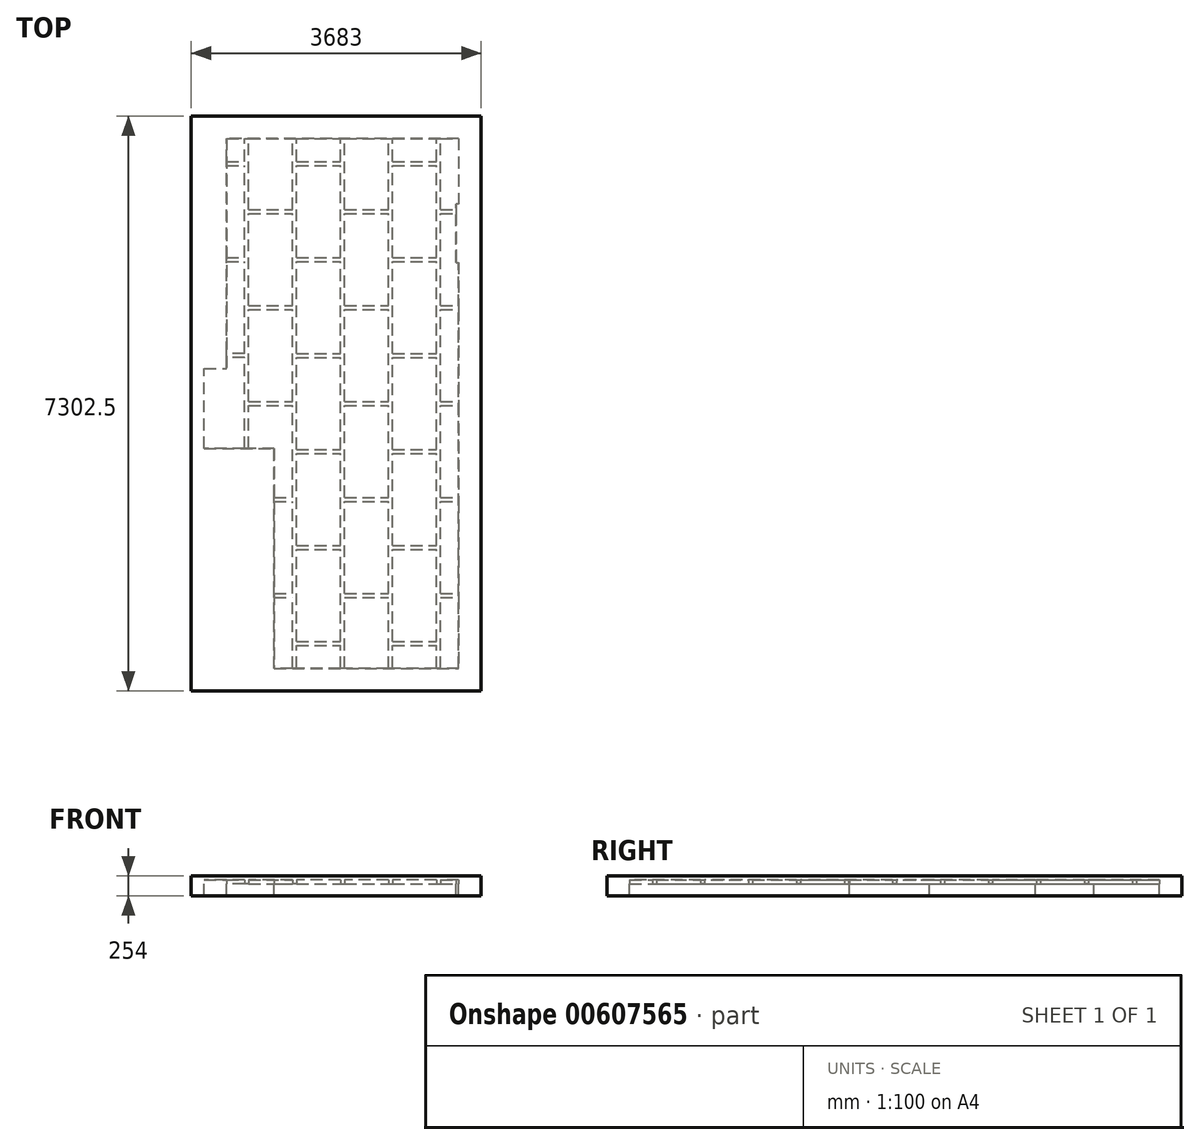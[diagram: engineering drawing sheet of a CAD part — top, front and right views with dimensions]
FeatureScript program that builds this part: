
annotation { "Feature Type Name" : "Feature", "Feature Type Description" : "" }
export const myFeature = defineFeature(function(context is Context, id is Id, definition is map)
    precondition{}
    {
        {
            var Q0;
            Q0=qCreatedBy(makeId("Top.planeOp"),FACE);
            var sketch = newSketch(context, id + "F0", { "sketchPlane" : qUnion([Q0])});
            skLineSegment(sketch, "E0", {"start": v(0, 0) * mm, "end": v(0, 5156.2) * mm});
            skLineSegment(sketch, "E1", {"start": v(0, 5156.2) * mm, "end": v(-34.92, 5156.2) * mm});
            skLineSegment(sketch, "E2", {"start": v(-34.92, 5156.2) * mm, "end": v(-34.92, 5899.15) * mm});
            skLineSegment(sketch, "E3", {"start": v(-34.92, 5899.15) * mm, "end": v(0, 5899.15) * mm});
            skLineSegment(sketch, "E4", {"start": v(0, 5899.15) * mm, "end": v(0, 6731) * mm});
            skLineSegment(sketch, "E5", {"start": v(0, 6731) * mm, "end": v(-2946.4, 6731) * mm});
            skLineSegment(sketch, "E6", {"start": v(-2946.4, 6731) * mm, "end": v(-2946.4, 3810) * mm});
            skLineSegment(sketch, "E7", {"start": v(-2946.4, 3810) * mm, "end": v(-3232.15, 3810) * mm});
            skLineSegment(sketch, "E8", {"start": v(-3232.15, 3810) * mm, "end": v(-3232.15, 2794) * mm});
            skLineSegment(sketch, "E9", {"start": v(-3232.15, 2794) * mm, "end": v(-2343.15, 2794) * mm});
            skLineSegment(sketch, "E10", {"start": v(-2343.15, 2794) * mm, "end": v(-2343.15, 0) * mm});
            skLineSegment(sketch, "E11", {"start": v(-2343.15, 0) * mm, "end": v(0, 0) * mm});
            skLineSegment(sketch, "E12", {"start": v(285.75, 7016.75) * mm, "end": v(285.75, -285.75) * mm});
            skLineSegment(sketch, "E13", {"start": v(285.75, -285.75) * mm, "end": v(-3397.25, -285.75) * mm});
            skLineSegment(sketch, "E14", {"start": v(285.75, 7016.75) * mm, "end": v(-3397.25, 7016.75) * mm});
            skLineSegment(sketch, "E15", {"start": v(-3397.25, 7016.75) * mm, "end": v(-3397.25, -285.75) * mm});
            skSolve(sketch);
        }
        {
            var Q0;
            Q0=makeQuery(id+"F0.imprint","IMPRINT",FACE,{"disambiguationData":[TD([[makeQuery(id+"F0.imprint","IMPRINT",EDGE,{"derivedFrom":sQuery(id+"F0.wireOp",EDGE,"E0")}),-1.0]])]});
            extrude(context, id + "F1", {"entities" : qUnion([Q0]), "oppositeDirection" : true, "depth" : 254 * mm, "offsetDistance" : 25.4 * mm});
        }
        {
            var Q0;
            Q0=qSketchRegion(id+"F0",true);
            var Q1;
            Q1=makeQuery(id+"F0.imprint","IMPRINT",FACE,{"disambiguationData":[TD([[makeQuery(id+"F0.imprint","IMPRINT",EDGE,{"derivedFrom":sQuery(id+"F0.wireOp",EDGE,"E0")}),1.0]])]});
            extrude(context, id + "F2", {"entities" : qUnion([Q0, Q1]), "operationType" : NewBodyOperationType.ADD, "oppositeDirection" : true, "depth" : 101.6 * mm, "offsetDistance" : 25.4 * mm});
        }
        {
            var Q0;
            Q0=makeQuery(id+"F2.opExtrude","CAP_FACE",FACE,{"disambiguationData":[OSD([sQuery(id+"F0.wireOp",EDGE,"E12"),sQuery(id+"F0.wireOp",EDGE,"E13"),sQuery(id+"F0.wireOp",EDGE,"E14"),sQuery(id+"F0.wireOp",EDGE,"E15")])],"isStart":false});
            var sketch = newSketch(context, id + "F3", { "sketchPlane" : qUnion([Q0])});
            skLineSegment(sketch, "E16.bottom", {"start": v(-2060.58, 0) * mm, "end": v(-2111.38, 0) * mm});
            skLineSegment(sketch, "E16.top", {"start": v(-2060.57, -6731) * mm, "end": v(-2111.37, -6731) * mm});
            skLineSegment(sketch, "E16.left", {"start": v(-2060.58, 0) * mm, "end": v(-2060.58, -292.1) * mm});
            skLineSegment(sketch, "E17.bottom", {"start": v(-1450.98, 0) * mm, "end": v(-1501.78, 0) * mm});
            skLineSegment(sketch, "E17.top", {"start": v(-1450.97, -6731) * mm, "end": v(-1501.77, -6731) * mm});
            skLineSegment(sketch, "E17.left", {"start": v(-1450.98, 0) * mm, "end": v(-1450.98, -901.7) * mm});
            skLineSegment(sketch, "E17.right", {"start": v(-1501.78, 0) * mm, "end": v(-1501.78, -292.1) * mm});
            skPoint(sketch, "E18.oppositeSnap0", {"position": v(-892.18, 0) * mm});
            skLineSegment(sketch, "E18.bottom", {"start": v(-841.38, 0) * mm, "end": v(-892.18, 0) * mm});
            skLineSegment(sketch, "E18.top", {"start": v(-841.37, -6731) * mm, "end": v(-892.17, -6731) * mm});
            skLineSegment(sketch, "E18.left", {"start": v(-841.38, 0) * mm, "end": v(-841.38, -292.1) * mm});
            skLineSegment(sketch, "E18.right", {"start": v(-892.18, 0) * mm, "end": v(-892.18, -901.7) * mm});
            skLineSegment(sketch, "E19.bottom", {"start": v(-282.58, 0) * mm, "end": v(-231.78, 0) * mm});
            skLineSegment(sketch, "E19.top", {"start": v(-282.57, -6731) * mm, "end": v(-231.77, -6731) * mm});
            skLineSegment(sketch, "E19.left", {"start": v(-282.58, 0) * mm, "end": v(-282.57, -292.1) * mm});
            skLineSegment(sketch, "E19.right", {"start": v(-231.78, 0) * mm, "end": v(-231.77, -901.7) * mm});
            skLineSegment(sketch, "E20.bottom", {"start": v(-2720.98, -2794) * mm, "end": v(-2670.18, -2794) * mm});
            skLineSegment(sketch, "E20.top", {"start": v(-2720.98, -6731) * mm, "end": v(-2670.18, -6731) * mm});
            skLineSegment(sketch, "E20.left", {"start": v(-2720.98, -2794) * mm, "end": v(-2720.98, -3949.7) * mm});
            skLineSegment(sketch, "E21.bottom", {"start": v(-231.77, -5829.3) * mm, "end": v(-34.92, -5829.3) * mm});
            skLineSegment(sketch, "E21.top", {"start": v(-2946.4, -6388.1) * mm, "end": v(-2720.97, -6388.1) * mm});
            skLineSegment(sketch, "E21.left", {"start": v(-2946.4, -6438.9) * mm, "end": v(-2946.4, -6388.1) * mm});
            skLineSegment(sketch, "E21.right", {"start": v(-34.92, -5829.3) * mm, "end": v(-34.92, -5778.5) * mm});
            skLineSegment(sketch, "E22.bottom", {"start": v(-231.77, -4559.3) * mm, "end": v(0, -4559.3) * mm});
            skLineSegment(sketch, "E22.top", {"start": v(-2946.4, -5219.7) * mm, "end": v(-2720.98, -5219.7) * mm});
            skLineSegment(sketch, "E22.left", {"start": v(-2946.4, -5168.9) * mm, "end": v(-2946.4, -5219.7) * mm});
            skLineSegment(sketch, "E22.right", {"start": v(0, -4559.3) * mm, "end": v(0, -4610.1) * mm});
            skLineSegment(sketch, "E23.bottom", {"start": v(-231.77, -2120.9) * mm, "end": v(0, -2120.9) * mm});
            skLineSegment(sketch, "E23.top", {"start": v(-2343.15, -2171.7) * mm, "end": v(-2111.38, -2171.7) * mm});
            skLineSegment(sketch, "E23.left", {"start": v(-2343.15, -2120.9) * mm, "end": v(-2343.15, -2171.7) * mm});
            skLineSegment(sketch, "E23.right", {"start": v(0, -2120.9) * mm, "end": v(0, -2171.7) * mm});
            skLineSegment(sketch, "E24.bottom", {"start": v(-231.77, -901.7) * mm, "end": v(0, -901.7) * mm});
            skLineSegment(sketch, "E24.top", {"start": v(-2343.15, -952.5) * mm, "end": v(-2111.38, -952.5) * mm});
            skLineSegment(sketch, "E24.left", {"start": v(-2343.15, -901.7) * mm, "end": v(-2343.15, -952.5) * mm});
            skLineSegment(sketch, "E24.right", {"start": v(0, -901.7) * mm, "end": v(0, -952.5) * mm});
            skLineSegment(sketch, "E25.trimOffspring", {"start": v(-2111.38, 0) * mm, "end": v(-2111.38, -901.7) * mm});
            skLineSegment(sketch, "E26.trimOffspring", {"start": v(-2343.15, -901.7) * mm, "end": v(-2111.38, -901.7) * mm});
            skLineSegment(sketch, "E27.trimOffspring", {"start": v(-2060.58, -342.9) * mm, "end": v(-1501.78, -342.9) * mm});
            skLineSegment(sketch, "E28.trimOffspring", {"start": v(-2060.58, -292.1) * mm, "end": v(-1501.78, -292.1) * mm});
            skLineSegment(sketch, "E29.trimOffspring", {"start": v(-1450.98, -952.5) * mm, "end": v(-892.18, -952.5) * mm});
            skLineSegment(sketch, "E30.trimOffspring", {"start": v(-1450.98, -901.7) * mm, "end": v(-892.18, -901.7) * mm});
            skLineSegment(sketch, "E31.trimOffspring", {"start": v(-841.38, -342.9) * mm, "end": v(-282.58, -342.9) * mm});
            skLineSegment(sketch, "E32.trimOffspring", {"start": v(-841.38, -292.1) * mm, "end": v(-282.58, -292.1) * mm});
            skLineSegment(sketch, "E33.trimOffspring", {"start": v(-231.77, -952.5) * mm, "end": v(0, -952.5) * mm});
            skLineSegment(sketch, "E34.trimOffspring", {"start": v(-2343.15, -2120.9) * mm, "end": v(-2111.38, -2120.9) * mm});
            skLineSegment(sketch, "E35.trimOffspring", {"start": v(-2060.57, -1562.1) * mm, "end": v(-1501.78, -1562.1) * mm});
            skLineSegment(sketch, "E36.trimOffspring", {"start": v(-2060.57, -1511.3) * mm, "end": v(-1501.78, -1511.3) * mm});
            skLineSegment(sketch, "E37.trimOffspring", {"start": v(-1450.98, -2171.7) * mm, "end": v(-892.18, -2171.7) * mm});
            skLineSegment(sketch, "E38.trimOffspring", {"start": v(-1450.98, -2120.9) * mm, "end": v(-892.18, -2120.9) * mm});
            skLineSegment(sketch, "E39.trimOffspring", {"start": v(-841.38, -1562.1) * mm, "end": v(-282.57, -1562.1) * mm});
            skLineSegment(sketch, "E40.trimOffspring", {"start": v(-841.38, -1511.3) * mm, "end": v(-282.57, -1511.3) * mm});
            skLineSegment(sketch, "E41.trimOffspring", {"start": v(-231.77, -2171.7) * mm, "end": v(0, -2171.7) * mm});
            skLineSegment(sketch, "E42.trimOffspring", {"start": v(-2670.18, -3340.1) * mm, "end": v(-2111.38, -3340.1) * mm});
            skLineSegment(sketch, "E43.trimOffspring", {"start": v(-2670.18, -5829.3) * mm, "end": v(-2670.18, -6731) * mm});
            skLineSegment(sketch, "E44.trimOffspring", {"start": v(-2670.18, -3390.9) * mm, "end": v(-2111.38, -3390.9) * mm});
            skLineSegment(sketch, "E45.trimOffspring", {"start": v(-2060.57, -2730.5) * mm, "end": v(-1501.77, -2730.5) * mm});
            skLineSegment(sketch, "E46.trimOffspring", {"start": v(-2060.57, -2781.3) * mm, "end": v(-1501.77, -2781.3) * mm});
            skLineSegment(sketch, "E47.trimOffspring", {"start": v(-1450.97, -3340.1) * mm, "end": v(-892.18, -3340.1) * mm});
            skLineSegment(sketch, "E48.trimOffspring", {"start": v(-1450.97, -3390.9) * mm, "end": v(-892.18, -3390.9) * mm});
            skLineSegment(sketch, "E49.trimOffspring", {"start": v(-841.37, -2730.5) * mm, "end": v(-282.57, -2730.5) * mm});
            skLineSegment(sketch, "E50.trimOffspring", {"start": v(-841.37, -2781.3) * mm, "end": v(-282.57, -2781.3) * mm});
            skLineSegment(sketch, "E51.trimOffspring", {"start": v(-231.77, -3340.1) * mm, "end": v(0, -3340.1) * mm});
            skLineSegment(sketch, "E52.trimOffspring", {"start": v(-231.77, -3390.9) * mm, "end": v(0, -3390.9) * mm});
            skLineSegment(sketch, "E53.trimOffspring", {"start": v(-2946.4, -5168.9) * mm, "end": v(-2720.98, -5168.9) * mm});
            skLineSegment(sketch, "E54.trimOffspring", {"start": v(-2670.18, -4610.1) * mm, "end": v(-2111.37, -4610.1) * mm});
            skLineSegment(sketch, "E55.trimOffspring", {"start": v(-2670.18, -4559.3) * mm, "end": v(-2111.37, -4559.3) * mm});
            skLineSegment(sketch, "E56.trimOffspring", {"start": v(-2060.57, -4000.5) * mm, "end": v(-1501.77, -4000.5) * mm});
            skLineSegment(sketch, "E57.trimOffspring", {"start": v(-2060.57, -3949.7) * mm, "end": v(-1501.77, -3949.7) * mm});
            skLineSegment(sketch, "E58.trimOffspring", {"start": v(-1450.97, -4610.1) * mm, "end": v(-892.17, -4610.1) * mm});
            skLineSegment(sketch, "E59.trimOffspring", {"start": v(-1450.97, -4559.3) * mm, "end": v(-892.17, -4559.3) * mm});
            skLineSegment(sketch, "E60.trimOffspring", {"start": v(-841.37, -4000.5) * mm, "end": v(-282.57, -4000.5) * mm});
            skLineSegment(sketch, "E61.trimOffspring", {"start": v(-841.37, -3949.7) * mm, "end": v(-282.57, -3949.7) * mm});
            skLineSegment(sketch, "E62.trimOffspring", {"start": v(-231.77, -4610.1) * mm, "end": v(0, -4610.1) * mm});
            skLineSegment(sketch, "E63.trimOffspring", {"start": v(-2670.18, -5778.5) * mm, "end": v(-2111.37, -5778.5) * mm});
            skLineSegment(sketch, "E64.trimOffspring", {"start": v(-2946.4, -6438.9) * mm, "end": v(-2720.98, -6438.9) * mm});
            skLineSegment(sketch, "E65.trimOffspring", {"start": v(-2060.57, -5168.9) * mm, "end": v(-1501.77, -5168.9) * mm});
            skLineSegment(sketch, "E66.trimOffspring", {"start": v(-2670.18, -5829.3) * mm, "end": v(-2111.37, -5829.3) * mm});
            skLineSegment(sketch, "E67.trimOffspring", {"start": v(-1450.97, -5778.5) * mm, "end": v(-892.17, -5778.5) * mm});
            skLineSegment(sketch, "E68.trimOffspring", {"start": v(-2060.57, -5219.7) * mm, "end": v(-1501.77, -5219.7) * mm});
            skLineSegment(sketch, "E69.trimOffspring", {"start": v(-841.37, -5168.9) * mm, "end": v(-282.57, -5168.9) * mm});
            skLineSegment(sketch, "E70.trimOffspring", {"start": v(-1450.97, -5829.3) * mm, "end": v(-892.17, -5829.3) * mm});
            skLineSegment(sketch, "E71.trimOffspring", {"start": v(-231.77, -5778.5) * mm, "end": v(-34.92, -5778.5) * mm});
            skLineSegment(sketch, "E72.trimOffspring", {"start": v(-841.37, -5219.7) * mm, "end": v(-282.57, -5219.7) * mm});
            skLineSegment(sketch, "E73", {"start": v(-2060.58, -6388.1) * mm, "end": v(-1501.77, -6388.1) * mm});
            skLineSegment(sketch, "E74", {"start": v(-2060.58, -6438.9) * mm, "end": v(-1501.77, -6438.9) * mm});
            skLineSegment(sketch, "E75", {"start": v(-2720.98, -3949.7) * mm, "end": v(-2946.4, -3949.7) * mm});
            skLineSegment(sketch, "E76", {"start": v(-2720.98, -4000.5) * mm, "end": v(-2946.4, -4000.5) * mm});
            skLineSegment(sketch, "E77", {"start": v(-841.37, -6388.1) * mm, "end": v(-282.57, -6388.1) * mm});
            skLineSegment(sketch, "E78", {"start": v(-841.37, -6438.9) * mm, "end": v(-282.57, -6438.9) * mm});
            skLineSegment(sketch, "E79.trimOffspring", {"start": v(-2060.58, -342.9) * mm, "end": v(-2060.57, -1511.3) * mm});
            skLineSegment(sketch, "E80.trimOffspring", {"start": v(-2111.38, -952.5) * mm, "end": v(-2111.38, -2120.9) * mm});
            skLineSegment(sketch, "E81.trimOffspring", {"start": v(-1501.78, -342.9) * mm, "end": v(-1501.78, -1511.3) * mm});
            skLineSegment(sketch, "E82.trimOffspring", {"start": v(-1450.98, -952.5) * mm, "end": v(-1450.98, -2120.9) * mm});
            skLineSegment(sketch, "E83.trimOffspring", {"start": v(-892.18, -952.5) * mm, "end": v(-892.18, -2120.9) * mm});
            skLineSegment(sketch, "E84.trimOffspring", {"start": v(-841.38, -342.9) * mm, "end": v(-841.38, -1511.3) * mm});
            skLineSegment(sketch, "E85.trimOffspring", {"start": v(-282.57, -342.9) * mm, "end": v(-282.57, -1511.3) * mm});
            skLineSegment(sketch, "E86.trimOffspring", {"start": v(-231.77, -952.5) * mm, "end": v(-231.77, -2120.9) * mm});
            skLineSegment(sketch, "E87.trimOffspring", {"start": v(-2060.57, -1562.1) * mm, "end": v(-2060.57, -2730.5) * mm});
            skLineSegment(sketch, "E88.trimOffspring", {"start": v(-1501.78, -1562.1) * mm, "end": v(-1501.77, -2730.5) * mm});
            skLineSegment(sketch, "E89.trimOffspring", {"start": v(-841.38, -1562.1) * mm, "end": v(-841.37, -2730.5) * mm});
            skLineSegment(sketch, "E90.trimOffspring", {"start": v(-282.57, -1562.1) * mm, "end": v(-282.57, -2730.5) * mm});
            skLineSegment(sketch, "E91.trimOffspring", {"start": v(-231.77, -2171.7) * mm, "end": v(-231.77, -3340.1) * mm});
            skLineSegment(sketch, "E92.trimOffspring", {"start": v(-892.18, -2171.7) * mm, "end": v(-892.18, -3340.1) * mm});
            skLineSegment(sketch, "E93.trimOffspring", {"start": v(-1450.98, -2171.7) * mm, "end": v(-1450.97, -3340.1) * mm});
            skLineSegment(sketch, "E94.trimOffspring", {"start": v(-2111.38, -2171.7) * mm, "end": v(-2111.38, -3340.1) * mm});
            skLineSegment(sketch, "E95.trimOffspring", {"start": v(-2060.57, -2781.3) * mm, "end": v(-2060.57, -3949.7) * mm});
            skLineSegment(sketch, "E96.trimOffspring", {"start": v(-1501.77, -2781.3) * mm, "end": v(-1501.77, -3949.7) * mm});
            skLineSegment(sketch, "E97.trimOffspring", {"start": v(-841.37, -2781.3) * mm, "end": v(-841.37, -3949.7) * mm});
            skLineSegment(sketch, "E98.trimOffspring", {"start": v(-282.57, -2781.3) * mm, "end": v(-282.57, -3949.7) * mm});
            skLineSegment(sketch, "E99.trimOffspring", {"start": v(-231.77, -3390.9) * mm, "end": v(-231.77, -4559.3) * mm});
            skLineSegment(sketch, "E100.trimOffspring", {"start": v(-892.18, -3390.9) * mm, "end": v(-892.17, -4559.3) * mm});
            skLineSegment(sketch, "E101.trimOffspring", {"start": v(-1450.97, -3390.9) * mm, "end": v(-1450.97, -4559.3) * mm});
            skLineSegment(sketch, "E102.trimOffspring", {"start": v(-2111.38, -3390.9) * mm, "end": v(-2111.37, -4559.3) * mm});
            skLineSegment(sketch, "E103.trimOffspring", {"start": v(-2060.57, -4000.5) * mm, "end": v(-2060.57, -5168.9) * mm});
            skLineSegment(sketch, "E104.trimOffspring", {"start": v(-1501.77, -4000.5) * mm, "end": v(-1501.77, -5168.9) * mm});
            skLineSegment(sketch, "E105.trimOffspring", {"start": v(-841.37, -4000.5) * mm, "end": v(-841.37, -5168.9) * mm});
            skLineSegment(sketch, "E106.trimOffspring", {"start": v(-282.57, -4000.5) * mm, "end": v(-282.57, -5168.9) * mm});
            skLineSegment(sketch, "E107.trimOffspring", {"start": v(-231.77, -4610.1) * mm, "end": v(-231.77, -5778.5) * mm});
            skLineSegment(sketch, "E108.trimOffspring", {"start": v(-282.57, -5219.7) * mm, "end": v(-282.57, -6388.1) * mm});
            skLineSegment(sketch, "E109.trimOffspring", {"start": v(-841.37, -5219.7) * mm, "end": v(-841.37, -6388.1) * mm});
            skLineSegment(sketch, "E110.trimOffspring", {"start": v(-892.17, -4610.1) * mm, "end": v(-892.17, -5778.5) * mm});
            skLineSegment(sketch, "E111.trimOffspring", {"start": v(-1450.97, -4610.1) * mm, "end": v(-1450.97, -5778.5) * mm});
            skLineSegment(sketch, "E112.trimOffspring", {"start": v(-1501.77, -5219.7) * mm, "end": v(-1501.77, -6388.1) * mm});
            skLineSegment(sketch, "E113.trimOffspring", {"start": v(-2060.57, -5219.7) * mm, "end": v(-2060.57, -6388.1) * mm});
            skLineSegment(sketch, "E114.trimOffspring", {"start": v(-2111.37, -4610.1) * mm, "end": v(-2111.37, -5778.5) * mm});
            skLineSegment(sketch, "E115.trimOffspring", {"start": v(-231.77, -5829.3) * mm, "end": v(-231.77, -6731) * mm});
            skLineSegment(sketch, "E116.trimOffspring", {"start": v(-282.57, -6438.9) * mm, "end": v(-282.57, -6731) * mm});
            skLineSegment(sketch, "E117.trimOffspring", {"start": v(-841.37, -6438.9) * mm, "end": v(-841.37, -6731) * mm});
            skLineSegment(sketch, "E118.trimOffspring", {"start": v(-892.17, -5829.3) * mm, "end": v(-892.17, -6731) * mm});
            skLineSegment(sketch, "E119.trimOffspring", {"start": v(-1450.97, -5829.3) * mm, "end": v(-1450.97, -6731) * mm});
            skLineSegment(sketch, "E120.trimOffspring", {"start": v(-1501.77, -6438.9) * mm, "end": v(-1501.77, -6731) * mm});
            skLineSegment(sketch, "E121.trimOffspring", {"start": v(-2060.57, -6438.9) * mm, "end": v(-2060.57, -6731) * mm});
            skLineSegment(sketch, "E122.trimOffspring", {"start": v(-2111.37, -5829.3) * mm, "end": v(-2111.37, -6731) * mm});
            skLineSegment(sketch, "E123.trimOffspring", {"start": v(-2720.98, -6438.9) * mm, "end": v(-2720.98, -6731) * mm});
            skLineSegment(sketch, "E124.trimOffspring", {"start": v(-2720.98, -4000.5) * mm, "end": v(-2720.98, -5168.9) * mm});
            skLineSegment(sketch, "E125.trimOffspring", {"start": v(-2720.98, -5219.7) * mm, "end": v(-2720.98, -6388.1) * mm});
            skLineSegment(sketch, "E126.trimOffspring", {"start": v(-2670.18, -2794) * mm, "end": v(-2670.18, -3340.1) * mm});
            skLineSegment(sketch, "E127.trimOffspring", {"start": v(-2670.18, -3390.9) * mm, "end": v(-2670.18, -4559.3) * mm});
            skLineSegment(sketch, "E128.trimOffspring", {"start": v(-2670.18, -4610.1) * mm, "end": v(-2670.18, -5778.5) * mm});
            skSolve(sketch);
        }
        {
            var Q0;
            {var subQ4=sQuery(id+"F3.wireOp",EDGE,"E20.left");Q0=makeQuery(id+"F3.imprint","IMPRINT",FACE,{"disambiguationData":[TD([[makeQuery(id+"F3.imprint","IMPRINT",EDGE,{"derivedFrom":subQ4}),-1.0]])]});}
            var Q1;
            {var subQ0=sQuery(id+"F3.wireOp",EDGE,"E53.trimOffspring");Q1=makeQuery(id+"F3.imprint","IMPRINT",FACE,{"disambiguationData":[TD([[makeQuery(id+"F3.imprint","IMPRINT",EDGE,{"derivedFrom":subQ0}),1.0]])]});}
            var Q2;
            {var subQ0=sQuery(id+"F3.wireOp",EDGE,"E21.top");Q2=makeQuery(id+"F3.imprint","IMPRINT",FACE,{"disambiguationData":[TD([[makeQuery(id+"F3.imprint","IMPRINT",EDGE,{"derivedFrom":subQ0}),1.0]])]});}
            var Q3;
            {var subQ0=sQuery(id+"F3.wireOp",EDGE,"E64.trimOffspring");Q3=makeQuery(id+"F3.imprint","IMPRINT",FACE,{"disambiguationData":[TD([[makeQuery(id+"F3.imprint","IMPRINT",EDGE,{"derivedFrom":subQ0}),-1.0]])]});}
            var Q4;
            {var subQ0=sQuery(id+"F3.wireOp",EDGE,"E43.trimOffspring");Q4=makeQuery(id+"F3.imprint","IMPRINT",FACE,{"disambiguationData":[TD([[makeQuery(id+"F3.imprint","IMPRINT",EDGE,{"derivedFrom":subQ0}),1.0]])]});}
            var Q5;
            Q5=makeQuery(id+"F3.imprint","IMPRINT",FACE,{"disambiguationData":[TD([[makeQuery(id+"F3.imprint","IMPRINT",EDGE,{"derivedFrom":sQuery(id+"F3.wireOp",EDGE,"E54.trimOffspring")}),-1.0]])]});
            var Q6;
            Q6=makeQuery(id+"F3.imprint","IMPRINT",FACE,{"disambiguationData":[TD([[makeQuery(id+"F3.imprint","IMPRINT",EDGE,{"derivedFrom":sQuery(id+"F3.wireOp",EDGE,"E44.trimOffspring")}),-1.0]])]});
            var Q7;
            {var subQ1=sQuery(id+"F3.wireOp",EDGE,"E23.top");Q7=makeQuery(id+"F3.imprint","IMPRINT",FACE,{"disambiguationData":[TD([[makeQuery(id+"F3.imprint","IMPRINT",EDGE,{"derivedFrom":subQ1}),-1.0]])]});}
            var Q8;
            {var subQ0=sQuery(id+"F3.wireOp",EDGE,"E24.top");Q8=makeQuery(id+"F3.imprint","IMPRINT",FACE,{"disambiguationData":[TD([[makeQuery(id+"F3.imprint","IMPRINT",EDGE,{"derivedFrom":subQ0}),-1.0]])]});}
            var Q9;
            {var subQ0=sQuery(id+"F3.wireOp",EDGE,"E25.trimOffspring");Q9=makeQuery(id+"F3.imprint","IMPRINT",FACE,{"disambiguationData":[TD([[makeQuery(id+"F3.imprint","IMPRINT",EDGE,{"derivedFrom":subQ0}),-1.0]])]});}
            var Q10;
            {var subQ0=sQuery(id+"F3.wireOp",EDGE,"E16.left");Q10=makeQuery(id+"F3.imprint","IMPRINT",FACE,{"disambiguationData":[TD([[makeQuery(id+"F3.imprint","IMPRINT",EDGE,{"derivedFrom":subQ0}),1.0]])]});}
            var Q11;
            Q11=makeQuery(id+"F3.imprint","IMPRINT",FACE,{"disambiguationData":[TD([[makeQuery(id+"F3.imprint","IMPRINT",EDGE,{"derivedFrom":sQuery(id+"F3.wireOp",EDGE,"E27.trimOffspring")}),-1.0]])]});
            var Q12;
            Q12=makeQuery(id+"F3.imprint","IMPRINT",FACE,{"disambiguationData":[TD([[makeQuery(id+"F3.imprint","IMPRINT",EDGE,{"derivedFrom":sQuery(id+"F3.wireOp",EDGE,"E35.trimOffspring")}),-1.0]])]});
            var Q13;
            Q13=makeQuery(id+"F3.imprint","IMPRINT",FACE,{"disambiguationData":[TD([[makeQuery(id+"F3.imprint","IMPRINT",EDGE,{"derivedFrom":sQuery(id+"F3.wireOp",EDGE,"E46.trimOffspring")}),-1.0]])]});
            var Q14;
            Q14=makeQuery(id+"F3.imprint","IMPRINT",FACE,{"disambiguationData":[TD([[makeQuery(id+"F3.imprint","IMPRINT",EDGE,{"derivedFrom":sQuery(id+"F3.wireOp",EDGE,"E56.trimOffspring")}),-1.0]])]});
            var Q15;
            Q15=makeQuery(id+"F3.imprint","IMPRINT",FACE,{"disambiguationData":[TD([[makeQuery(id+"F3.imprint","IMPRINT",EDGE,{"derivedFrom":sQuery(id+"F3.wireOp",EDGE,"E68.trimOffspring")}),-1.0]])]});
            var Q16;
            Q16=makeQuery(id+"F3.imprint","IMPRINT",FACE,{"disambiguationData":[TD([[makeQuery(id+"F3.imprint","IMPRINT",EDGE,{"derivedFrom":sQuery(id+"F3.wireOp",EDGE,"E74")}),-1.0]])]});
            var Q17;
            Q17=makeQuery(id+"F3.imprint","IMPRINT",FACE,{"disambiguationData":[TD([[makeQuery(id+"F3.imprint","IMPRINT",EDGE,{"derivedFrom":sQuery(id+"F3.wireOp",EDGE,"E70.trimOffspring")}),-1.0]])]});
            var Q18;
            Q18=makeQuery(id+"F3.imprint","IMPRINT",FACE,{"disambiguationData":[TD([[makeQuery(id+"F3.imprint","IMPRINT",EDGE,{"derivedFrom":sQuery(id+"F3.wireOp",EDGE,"E58.trimOffspring")}),-1.0]])]});
            var Q19;
            Q19=makeQuery(id+"F3.imprint","IMPRINT",FACE,{"disambiguationData":[TD([[makeQuery(id+"F3.imprint","IMPRINT",EDGE,{"derivedFrom":sQuery(id+"F3.wireOp",EDGE,"E48.trimOffspring")}),-1.0]])]});
            var Q20;
            Q20=makeQuery(id+"F3.imprint","IMPRINT",FACE,{"disambiguationData":[TD([[makeQuery(id+"F3.imprint","IMPRINT",EDGE,{"derivedFrom":sQuery(id+"F3.wireOp",EDGE,"E37.trimOffspring")}),-1.0]])]});
            var Q21;
            Q21=makeQuery(id+"F3.imprint","IMPRINT",FACE,{"disambiguationData":[TD([[makeQuery(id+"F3.imprint","IMPRINT",EDGE,{"derivedFrom":sQuery(id+"F3.wireOp",EDGE,"E29.trimOffspring")}),-1.0]])]});
            var Q22;
            {var subQ0=sQuery(id+"F3.wireOp",EDGE,"E17.left");Q22=makeQuery(id+"F3.imprint","IMPRINT",FACE,{"disambiguationData":[TD([[makeQuery(id+"F3.imprint","IMPRINT",EDGE,{"derivedFrom":subQ0}),1.0]])]});}
            var Q23;
            {var subQ0=sQuery(id+"F3.wireOp",EDGE,"E18.left");Q23=makeQuery(id+"F3.imprint","IMPRINT",FACE,{"disambiguationData":[TD([[makeQuery(id+"F3.imprint","IMPRINT",EDGE,{"derivedFrom":subQ0}),1.0]])]});}
            var Q24;
            Q24=makeQuery(id+"F3.imprint","IMPRINT",FACE,{"disambiguationData":[TD([[makeQuery(id+"F3.imprint","IMPRINT",EDGE,{"derivedFrom":sQuery(id+"F3.wireOp",EDGE,"E31.trimOffspring")}),-1.0]])]});
            var Q25;
            Q25=makeQuery(id+"F3.imprint","IMPRINT",FACE,{"disambiguationData":[TD([[makeQuery(id+"F3.imprint","IMPRINT",EDGE,{"derivedFrom":sQuery(id+"F3.wireOp",EDGE,"E39.trimOffspring")}),-1.0]])]});
            var Q26;
            Q26=makeQuery(id+"F3.imprint","IMPRINT",FACE,{"disambiguationData":[TD([[makeQuery(id+"F3.imprint","IMPRINT",EDGE,{"derivedFrom":sQuery(id+"F3.wireOp",EDGE,"E50.trimOffspring")}),-1.0]])]});
            var Q27;
            Q27=makeQuery(id+"F3.imprint","IMPRINT",FACE,{"disambiguationData":[TD([[makeQuery(id+"F3.imprint","IMPRINT",EDGE,{"derivedFrom":sQuery(id+"F3.wireOp",EDGE,"E60.trimOffspring")}),-1.0]])]});
            var Q28;
            Q28=makeQuery(id+"F3.imprint","IMPRINT",FACE,{"disambiguationData":[TD([[makeQuery(id+"F3.imprint","IMPRINT",EDGE,{"derivedFrom":sQuery(id+"F3.wireOp",EDGE,"E72.trimOffspring")}),-1.0]])]});
            var Q29;
            Q29=makeQuery(id+"F3.imprint","IMPRINT",FACE,{"disambiguationData":[TD([[makeQuery(id+"F3.imprint","IMPRINT",EDGE,{"derivedFrom":sQuery(id+"F3.wireOp",EDGE,"E78")}),-1.0]])]});
            var Q30;
            {var subQ5=sQuery(id+"F3.wireOp",EDGE,"E21.bottom");Q30=makeQuery(id+"F3.imprint","IMPRINT",FACE,{"disambiguationData":[TD([[makeQuery(id+"F3.imprint","IMPRINT",EDGE,{"derivedFrom":subQ5}),-1.0]])]});}
            var Q31;
            {var subQ4=sQuery(id+"F3.wireOp",EDGE,"E62.trimOffspring");Q31=makeQuery(id+"F3.imprint","IMPRINT",FACE,{"disambiguationData":[TD([[makeQuery(id+"F3.imprint","IMPRINT",EDGE,{"derivedFrom":subQ4}),-1.0]])]});}
            var Q32;
            {var subQ0=sQuery(id+"F3.wireOp",EDGE,"E22.bottom");Q32=makeQuery(id+"F3.imprint","IMPRINT",FACE,{"disambiguationData":[TD([[makeQuery(id+"F3.imprint","IMPRINT",EDGE,{"derivedFrom":subQ0}),1.0]])]});}
            var Q33;
            {var subQ0=sQuery(id+"F3.wireOp",EDGE,"E41.trimOffspring");Q33=makeQuery(id+"F3.imprint","IMPRINT",FACE,{"disambiguationData":[TD([[makeQuery(id+"F3.imprint","IMPRINT",EDGE,{"derivedFrom":subQ0}),-1.0]])]});}
            var Q34;
            {var subQ0=sQuery(id+"F3.wireOp",EDGE,"E23.bottom");Q34=makeQuery(id+"F3.imprint","IMPRINT",FACE,{"disambiguationData":[TD([[makeQuery(id+"F3.imprint","IMPRINT",EDGE,{"derivedFrom":subQ0}),1.0]])]});}
            var Q35;
            {var subQ0=sQuery(id+"F3.wireOp",EDGE,"E19.right");Q35=makeQuery(id+"F3.imprint","IMPRINT",FACE,{"disambiguationData":[TD([[makeQuery(id+"F3.imprint","IMPRINT",EDGE,{"derivedFrom":subQ0}),1.0]])]});}
            extrude(context, id + "F4", {"entities" : qUnion([Q0, Q1, Q2, Q3, Q4, Q5, Q6, Q7, Q8, Q9, Q10, Q11, Q12, Q13, Q14, Q15, Q16, Q17, Q18, Q19, Q20, Q21, Q22, Q23, Q24, Q25, Q26, Q27, Q28, Q29, Q30, Q31, Q32, Q33, Q34, Q35]), "operationType" : NewBodyOperationType.REMOVE, "oppositeDirection" : true, "depth" : 50.8 * mm, "offsetDistance" : 25.4 * mm});
        }
    });
